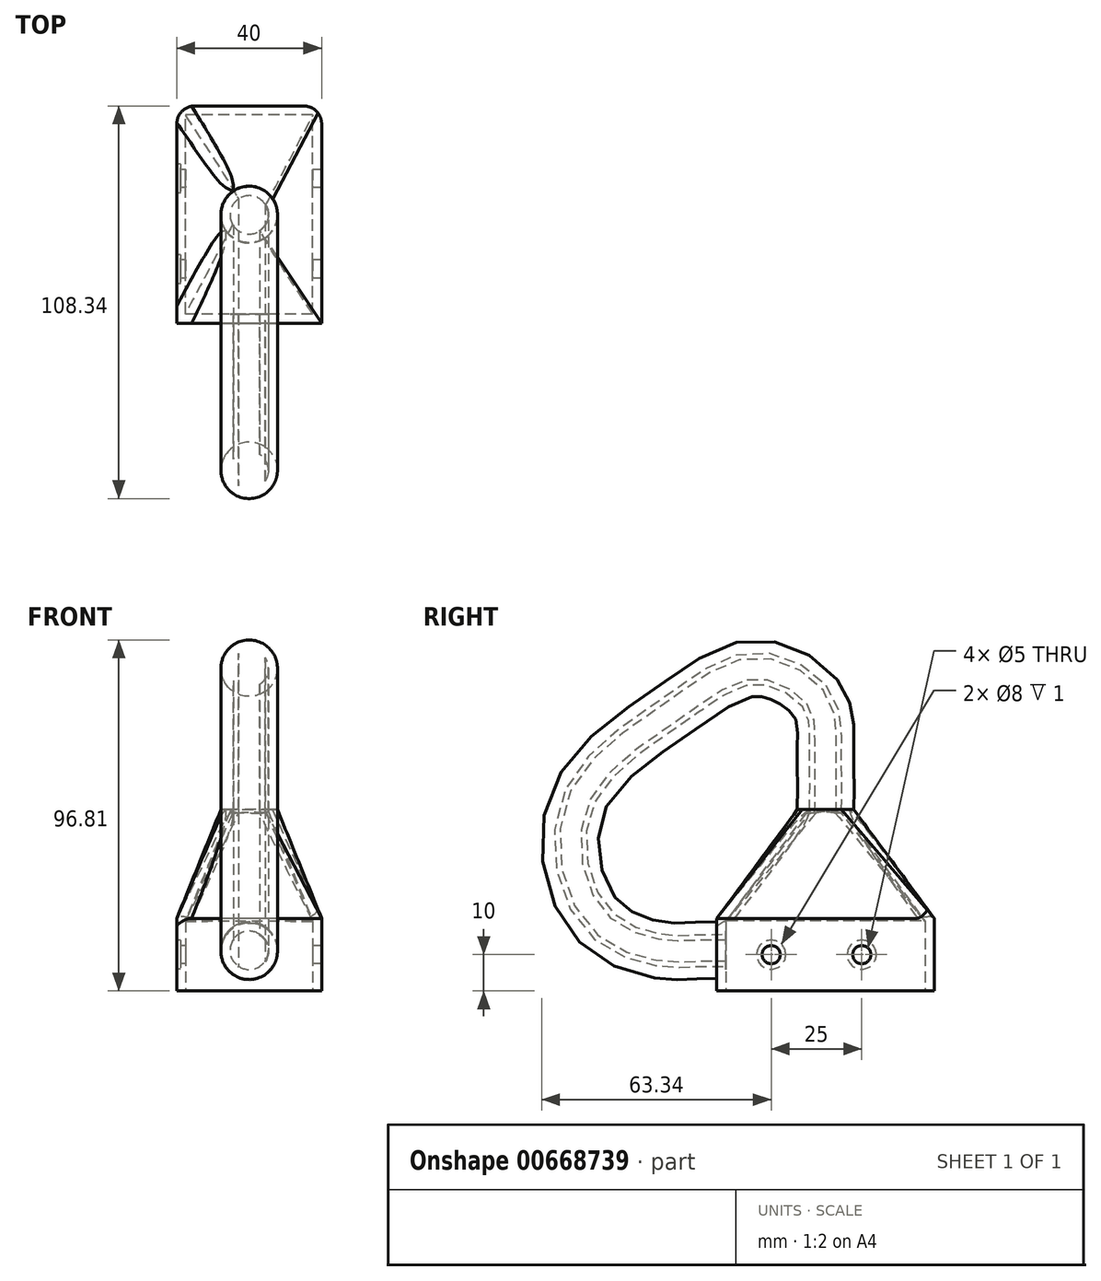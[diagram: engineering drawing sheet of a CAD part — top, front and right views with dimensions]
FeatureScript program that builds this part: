
annotation { "Feature Type Name" : "Feature", "Feature Type Description" : "" }
export const myFeature = defineFeature(function(context is Context, id is Id, definition is map)
    precondition{}
    {
        {
            var Q0;
            Q0=qCreatedBy(makeId("Top.planeOp"),FACE);
            var sketch = newSketch(context, id + "F0", { "sketchPlane" : qUnion([Q0])});
            skLineSegment(sketch, "E0.bottom", {"start": v(20, -30) * mm, "end": v(-20, -30) * mm});
            skLineSegment(sketch, "E0.top", {"start": v(20, 30) * mm, "end": v(-20, 30) * mm});
            skLineSegment(sketch, "E0.left", {"start": v(20, -30) * mm, "end": v(20, 30) * mm});
            skLineSegment(sketch, "E0.right", {"start": v(-20, -30) * mm, "end": v(-20, 30) * mm});
            skLineSegment(sketch, "E1", {"start": v(-20, 0) * mm, "end": v(20, 0) * mm, "construction": true});
            skLineSegment(sketch, "E2", {"start": v(0, 30) * mm, "end": v(0, -30) * mm, "construction": true});
            skSolve(sketch);
        }
        {
            var Q0;
            Q0 = qSketchRegion(id + "F0", true);
            extrude(context, id + "F1", {"entities" : qUnion([Q0]), "depth" : 20 * mm, "offsetDistance" : 25 * mm});
        }
        {
            var Q0;
            Q0=qCreatedBy(makeId("Top.planeOp"),FACE);
            cPlane(context, id + "F2", {"entities" : qUnion([Q0]), "cplaneType" : CPlaneType.OFFSET, "offset" : 50 * mm, "width" : 150 * mm, "height" : 150 * mm});
        }
        {
            var Q0;
            Q0=qCreatedBy(id+"F2.planeOp",FACE);
            var sketch = newSketch(context, id + "F3", { "sketchPlane" : qUnion([Q0])});
            skCircle(sketch, "E3", {"center": v(0, 0) * mm, "radius": 7.8 * mm});
            skSolve(sketch);
        }
        {
            var Q1;
            Q1=makeQuery(id+"F1.opExtrude","CAP_FACE",FACE,{"disambiguationData":[OSD([sQuery(id+"F0.wireOp",EDGE,"E0.bottom"),sQuery(id+"F0.wireOp",EDGE,"E0.top"),sQuery(id+"F0.wireOp",EDGE,"E0.left"),sQuery(id+"F0.wireOp",EDGE,"E0.right")])],"isStart":false});
            var Q2;
            Q2=makeQuery(id+"F3.imprint","IMPRINT",FACE,{"disambiguationData":[TD([[makeQuery(id+"F3.imprint","IMPRINT",EDGE,{"derivedFrom":sQuery(id+"F3.wireOp",EDGE,"E3")}),1.0]])]});
            loft(context, id + "F4", {"operationType" : NewBodyOperationType.ADD, "sheetProfilesArray" : [{ "sheetProfileEntities" : qUnion([Q1]) }, { "sheetProfileEntities" : qUnion([Q2]) }]});
        }
        {
            var Q0;
            Q0=qCreatedBy(makeId("Right.planeOp"),FACE);
            var sketch = newSketch(context, id + "F5", { "sketchPlane" : qUnion([Q0])});
            skFitSpline(sketch, "E4", {"points": [v(0, 49.82) * mm, v(0, 66.85) * mm, v(-2.16, 80.03) * mm, v(-19.09, 89.03) * mm, v(-41.63, 77.61) * mm, v(-68.5, 52.16) * mm, v(-63, 19.56) * mm, v(-43.12, 11) * mm, v(-29.8, 11.21) * mm], "startDerivative": vector(6.85, 157.64) * mm, "endDerivative": vector(207.31, -3.18) * mm});
            skSolve(sketch);
        }
        {
            var Q0;
            Q0=makeQuery(id+"F4.opLoft","CAP_FACE",FACE,{"disambiguationData":[OSD([makeQuery(id+"F3.imprint","IMPRINT",FACE,{"disambiguationData":[TD([[makeQuery(id+"F3.imprint","IMPRINT",EDGE,{"derivedFrom":sQuery(id+"F3.wireOp",EDGE,"E3")}),1.0]])]})])],"isStart":true});
            var Q1;
            Q1 = qConstructionFilter(qBodyType(qCreatedBy(id + "F5" ,EDGE), BodyType.WIRE), ConstructionObject.NO);
            sweep(context, id + "F6", {"operationType" : NewBodyOperationType.ADD, "profiles" : qUnion([Q0]), "path" : qUnion([Q1])});
        }
        {
            var Q0;
            Q0=makeQuery(id+"F1.opExtrude","CAP_FACE",FACE,{"disambiguationData":[OSD([sQuery(id+"F0.wireOp",EDGE,"E0.bottom"),sQuery(id+"F0.wireOp",EDGE,"E0.top"),sQuery(id+"F0.wireOp",EDGE,"E0.left"),sQuery(id+"F0.wireOp",EDGE,"E0.right")])],"isStart":true});
            shell(context, id + "F7", {"entities" : qUnion([Q0]), "thickness" : 2.5 * mm});
        }
        {
            var Q0;
            Q0=makeQuery(id+"F4.opLoft","SWEPT_EDGE",EDGE,{"disambiguationData":[OSD([sQuery(id+"F0.wireOp",EDGE,"E0.bottom"),sQuery(id+"F0.wireOp",EDGE,"E0.top"),sQuery(id+"F0.wireOp",EDGE,"E0.left"),sQuery(id+"F3.wireOp",EDGE,"E3")])]});
            var Q1;
            Q1=makeQuery(id+"F1.opExtrude","SWEPT_EDGE",EDGE,{"disambiguationData":[OSD([sQuery(id+"F0.wireOp",EDGE,"E0.top"),sQuery(id+"F0.wireOp",EDGE,"E0.left")])]});
            var Q2;
            Q2=makeQuery(id+"F4.opLoft","SWEPT_EDGE",EDGE,{"disambiguationData":[OSD([sQuery(id+"F0.wireOp",EDGE,"E0.top"),sQuery(id+"F0.wireOp",EDGE,"E0.left"),sQuery(id+"F0.wireOp",EDGE,"E0.right"),sQuery(id+"F3.wireOp",EDGE,"E3")])]});
            var Q3;
            Q3=makeQuery(id+"F1.opExtrude","SWEPT_EDGE",EDGE,{"disambiguationData":[OSD([sQuery(id+"F0.wireOp",EDGE,"E0.top"),sQuery(id+"F0.wireOp",EDGE,"E0.right")])]});
            fillet(context, id + "F8", {"entities" : qUnion([Q0, Q1, Q2, Q3]), "radius" : 5 * mm, "tangentPropagation" : true, "allowEdgeOverflow" : false});
        }
        {
            var Q0;
            Q0=makeQuery(id+"F1.opExtrude","SWEPT_FACE",FACE,{"disambiguationData":[OSD([sQuery(id+"F0.wireOp",EDGE,"E0.right")])]});
            var sketch = newSketch(context, id + "F9", { "sketchPlane" : qUnion([Q0])});
            skPoint(sketch, "E5", {"position": v(-10, 10) * mm});
            skPoint(sketch, "E6", {"position": v(15, 10) * mm});
            skSolve(sketch);
        }
        {
            var Q0;
            Q0=sQuery(id+"F9.wireOp",VERTEX,"E5");
            var Q1;
            Q1=sQuery(id+"F9.wireOp",VERTEX,"E6");
            var Q2;
            Q2=makeQuery(id+"F1.opExtrude","SWEPT_BODY",BODY,{"disambiguationData":[OSD([sQuery(id+"F0.wireOp",EDGE,"E0.bottom"),sQuery(id+"F0.wireOp",EDGE,"E0.top"),sQuery(id+"F0.wireOp",EDGE,"E0.left"),sQuery(id+"F0.wireOp",EDGE,"E0.right")])]});
            hole(context, id + "F10", {"style" : HoleStyle.C_BORE, "endStyle" : HoleEndStyle.THROUGH, "holeDiameter" : 5 * mm, "cBoreDiameter" : 8 * mm, "cBoreDepth" : 1 * mm, "majorDiameter" : 5 * mm, "isTappedThrough" : true, "tappedDepth" : 12 * mm, "tapClearance" : 3, "locations" : qUnion([Q0, Q1]), "scope" : qUnion([Q2])});
        }
    });
